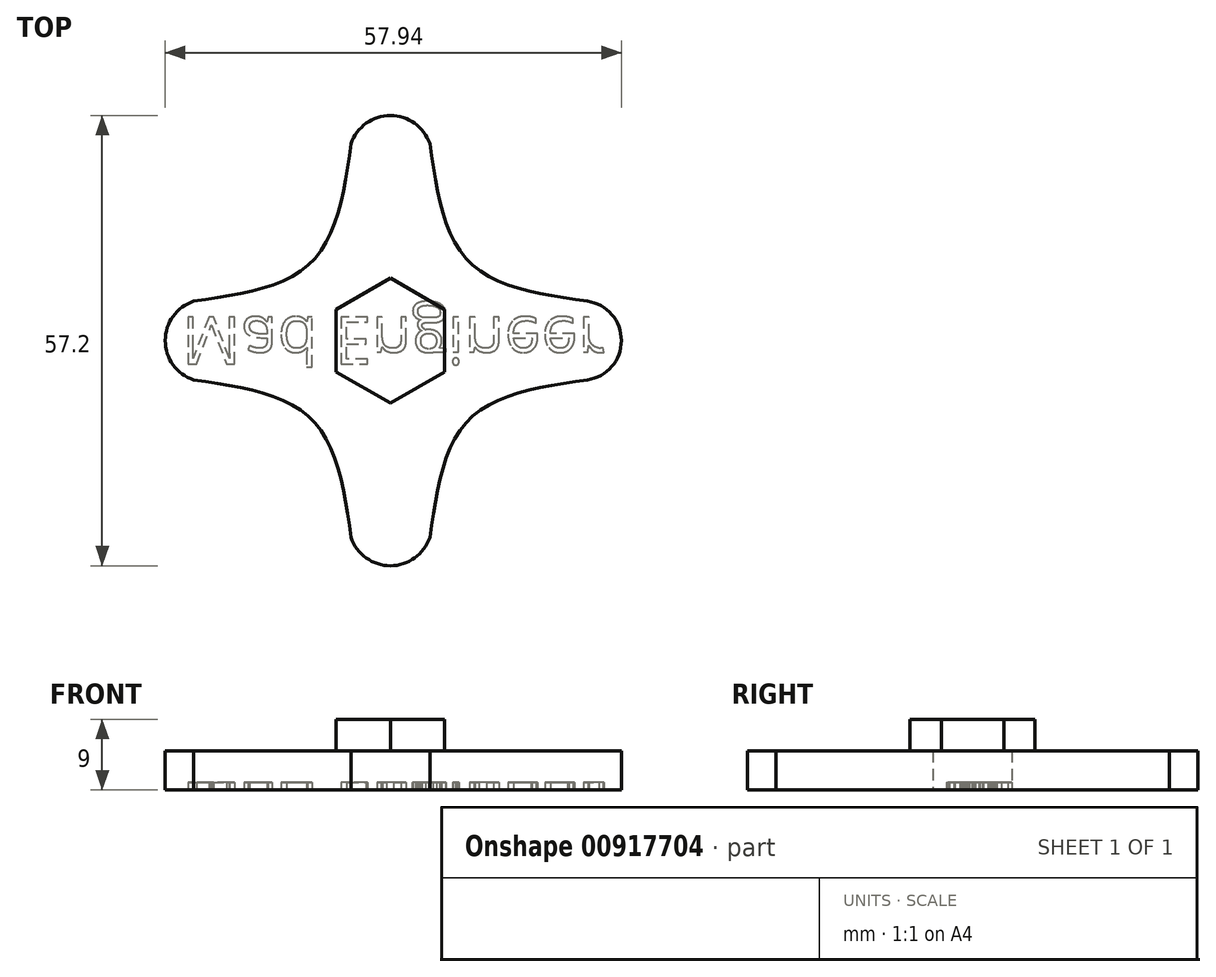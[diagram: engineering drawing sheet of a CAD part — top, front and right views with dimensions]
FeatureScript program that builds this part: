
annotation { "Feature Type Name" : "Feature", "Feature Type Description" : "" }
export const myFeature = defineFeature(function(context is Context, id is Id, definition is map)
    precondition{}
    {
        {
            var Q0;
            Q0=qCreatedBy(makeId("Top.planeOp"),FACE);
            var sketch = newSketch(context, id + "F0", { "sketchPlane" : qUnion([Q0])});
            skArc(sketch, "E0", {"start": v(-5, 25) * mm, "mid": v(0, 28.6) * mm, "end": v(5, 25) * mm});
            skArc(sketch, "E1", {"start": v(-25, 5) * mm, "mid": v(-28.6, 0) * mm, "end": v(-25, -5) * mm});
            skFitSpline(sketch, "E2", {"points": [v(-25, 5) * mm, v(-10, 10) * mm, v(-5, 25) * mm], "startDerivative": vector(35, 5) * mm, "endDerivative": vector(5, 35) * mm});
            skFitSpline(sketch, "E3", {"points": [v(5, 25) * mm, v(10, 10) * mm, v(25, 5) * mm], "startDerivative": vector(5, -35) * mm, "endDerivative": vector(35, -5) * mm});
            skArc(sketch, "E4", {"start": v(25, 5) * mm, "mid": v(29.34, 0) * mm, "end": v(25, -5) * mm});
            skArc(sketch, "E5", {"start": v(5, -25) * mm, "mid": v(0, -28.6) * mm, "end": v(-5, -25) * mm});
            skFitSpline(sketch, "E6", {"points": [v(-25, -5) * mm, v(-10, -10) * mm, v(-5, -25) * mm], "startDerivative": vector(35, -5) * mm, "endDerivative": vector(5, -35) * mm});
            skFitSpline(sketch, "E7", {"points": [v(5, -25) * mm, v(10, -10) * mm, v(25, -5) * mm], "startDerivative": vector(5.01, 34.97) * mm, "endDerivative": vector(34.99, 5.2) * mm});
            skSolve(sketch);
        }
        {
            var Q0;
            Q0 = qSketchRegion(id + "F0", true);
            extrude(context, id + "F1", {"entities" : qUnion([Q0]), "depth" : 5 * mm, "offsetDistance" : 25 * mm});
        }
        {
            var Q0;
            Q0=makeQuery(id+"F1.opExtrude","CAP_FACE",FACE,{"disambiguationData":[OSD([sQuery(id+"F0.wireOp",EDGE,"E0"),sQuery(id+"F0.wireOp",EDGE,"E1"),sQuery(id+"F0.wireOp",EDGE,"E2"),sQuery(id+"F0.wireOp",EDGE,"E3"),sQuery(id+"F0.wireOp",EDGE,"E4"),sQuery(id+"F0.wireOp",EDGE,"E5"),sQuery(id+"F0.wireOp",EDGE,"E6"),sQuery(id+"F0.wireOp",EDGE,"E7")])],"isStart":false});
            var sketch = newSketch(context, id + "F2", { "sketchPlane" : qUnion([Q0])});
            skCircle(sketch, "E8.cCircle", {"center": v(0, 0) * mm, "radius": 6.88 * mm, "construction": true});
            skLineSegment(sketch, "E8.0", {"start": v(0, 7.94) * mm, "end": v(6.87, 3.97) * mm});
            skLineSegment(sketch, "E8.1", {"start": v(6.87, 3.97) * mm, "end": v(6.87, -3.97) * mm});
            skLineSegment(sketch, "E8.2", {"start": v(6.88, -3.97) * mm, "end": v(0, -7.94) * mm});
            skLineSegment(sketch, "E8.3", {"start": v(0, -7.94) * mm, "end": v(-6.87, -3.97) * mm});
            skLineSegment(sketch, "E8.4", {"start": v(-6.88, -3.97) * mm, "end": v(-6.88, 3.97) * mm});
            skLineSegment(sketch, "E8.5", {"start": v(-6.87, 3.97) * mm, "end": v(0, 7.94) * mm});
            skPoint(sketch, "E8.0.midPoint", {"position": v(3.44, 5.95) * mm});
            skSolve(sketch);
        }
        {
            var Q0;
            Q0 = qSketchRegion(id + "F2", true);
            extrude(context, id + "F3", {"entities" : qUnion([Q0]), "operationType" : NewBodyOperationType.ADD, "depth" : 4 * mm, "offsetDistance" : 25 * mm});
        }
        {
            var Q0;
            Q0=makeQuery(id+"F1.opExtrude","CAP_FACE",FACE,{"disambiguationData":[OSD([sQuery(id+"F0.wireOp",EDGE,"E0"),sQuery(id+"F0.wireOp",EDGE,"E1"),sQuery(id+"F0.wireOp",EDGE,"E2"),sQuery(id+"F0.wireOp",EDGE,"E3"),sQuery(id+"F0.wireOp",EDGE,"E4"),sQuery(id+"F0.wireOp",EDGE,"E5"),sQuery(id+"F0.wireOp",EDGE,"E6"),sQuery(id+"F0.wireOp",EDGE,"E7")])],"isStart":true});
            var sketch = newSketch(context, id + "F4", { "sketchPlane" : qUnion([Q0])});
            skText(sketch, "E9", { "text": "Mad Engineer", "fontName": "OpenSans-Regular.ttf"});
            const initialGuessF4  = {"E9": [-0.0265, -0.003, 1, 0, 0.006]};
            skSetInitialGuess(sketch, initialGuessF4);
            skSolve(sketch);
        }
        {
            var Q0;
            Q0 = qSketchRegion(id + "F4", true);
            extrude(context, id + "F5", {"entities" : qUnion([Q0]), "operationType" : NewBodyOperationType.REMOVE, "oppositeDirection" : true, "depth" : 1 * mm, "offsetDistance" : 25 * mm});
        }
    });
